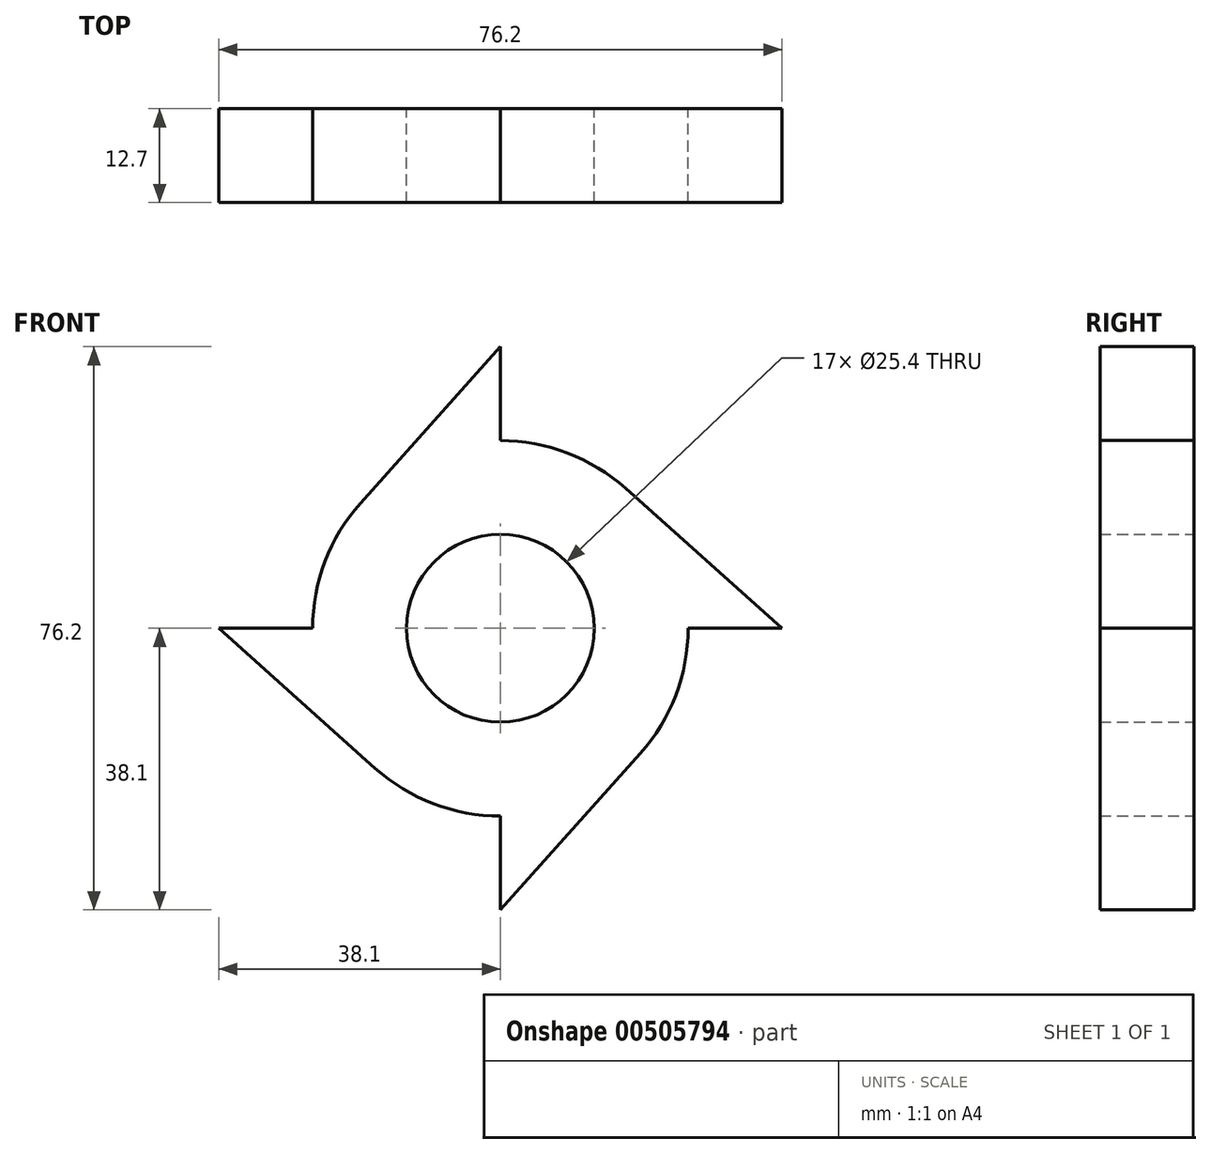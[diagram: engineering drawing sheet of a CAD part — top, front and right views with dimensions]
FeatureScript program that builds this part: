
annotation { "Feature Type Name" : "Feature", "Feature Type Description" : "" }
export const myFeature = defineFeature(function(context is Context, id is Id, definition is map)
    precondition{}
    {
        {
            var Q0;
            Q0=qCreatedBy(makeId("Front.planeOp"),FACE);
            var sketch = newSketch(context, id + "F0", { "sketchPlane" : qUnion([Q0])});
            skCircle(sketch, "E0", {"center": v(0, 0) * mm, "radius": 25.4 * mm});
            skLineSegment(sketch, "E1", {"start": v(0, 25.4) * mm, "end": v(0, 38.1) * mm});
            skLineSegment(sketch, "E2", {"start": v(0, 38.1) * mm, "end": v(-18.93, 16.93) * mm});
            skLineSegment(sketch, "E3", {"start": v(-25.4, 0) * mm, "end": v(-38.1, 0) * mm});
            skLineSegment(sketch, "E4", {"start": v(-38.1, 0) * mm, "end": v(-16.93, -18.93) * mm});
            skLineSegment(sketch, "E5", {"start": v(0, -25.4) * mm, "end": v(0, -38.1) * mm});
            skLineSegment(sketch, "E6", {"start": v(0, -38.1) * mm, "end": v(18.93, -16.93) * mm});
            skLineSegment(sketch, "E7", {"start": v(25.4, 0) * mm, "end": v(38.1, 0) * mm});
            skLineSegment(sketch, "E8", {"start": v(38.1, 0) * mm, "end": v(16.93, 18.93) * mm});
            skCircle(sketch, "E9", {"center": v(0, 0) * mm, "radius": 12.7 * mm});
            skSolve(sketch);
        }
        {
            var Q0;
            Q0=makeQuery(id+"F0.imprint","IMPRINT",FACE,{"disambiguationData":[TD([[makeQuery(id+"F0.imprint","IMPRINT",EDGE,{"derivedFrom":sQuery(id+"F0.wireOp",EDGE,"E9")}),-1.0]])]});
            var Q1;
            {var subQ0=sQuery(id+"F0.wireOp",EDGE,"E1");Q1=makeQuery(id+"F0.imprint","IMPRINT",FACE,{"disambiguationData":[TD([[makeQuery(id+"F0.imprint","IMPRINT",EDGE,{"derivedFrom":subQ0}),1.0]])]});}
            var Q2;
            {var subQ0=sQuery(id+"F0.wireOp",EDGE,"E7");Q2=makeQuery(id+"F0.imprint","IMPRINT",FACE,{"disambiguationData":[TD([[makeQuery(id+"F0.imprint","IMPRINT",EDGE,{"derivedFrom":subQ0}),1.0]])]});}
            var Q3;
            {var subQ0=sQuery(id+"F0.wireOp",EDGE,"E5");Q3=makeQuery(id+"F0.imprint","IMPRINT",FACE,{"disambiguationData":[TD([[makeQuery(id+"F0.imprint","IMPRINT",EDGE,{"derivedFrom":subQ0}),1.0]])]});}
            var Q4;
            {var subQ0=sQuery(id+"F0.wireOp",EDGE,"E3");Q4=makeQuery(id+"F0.imprint","IMPRINT",FACE,{"disambiguationData":[TD([[makeQuery(id+"F0.imprint","IMPRINT",EDGE,{"derivedFrom":subQ0}),1.0]])]});}
            extrude(context, id + "F1", {"entities" : qUnion([Q0, Q1, Q2, Q3, Q4]), "depth" : 12.7 * mm, "offsetDistance" : 25.4 * mm});
        }
    });
